# Revit family: Faucet_Touchless-Lavatory-KOHLER-Strayt-K-104S36-1
name_source: partatom
category: Plumbing Fixtures
units: mm (PartAtom-declared; Revit-internal decimal feet)

## family parameters
Cut with Voids When Loaded = No
Host = Face
Maintain Annotation Orientation = No
OmniClass Number = 23.31.11.00
OmniClass Title = Faucets
Part Type = Normal
Room Calculation Point = No
Round Connector Dimension = Use Diameter
Shared = No

## types (2) — shared parameters
ADA Compliant = Yes
Assembly Code = D2010
CW Connection = Yes
Cold Water Inlet = Cold Water Inlet
Date Modified = 06/20/2025
Default Elevation = 36"
Drain Included = Yes
Finish = Kohler-Metal-CP-Polished_Chrome
HW Connection = Yes
Height = 5 7/16"
Hot Water Inlet = Hot Water Inlet
Length = 5 3/16"
Manufacturer = Kohler Co.
Master Format 2014 = 22 41 39
Master Format 2014 Name = Residential Faucets, Supplies, and Trim
Material = Premium Metal Construction
Pressure = 60.00 psi
Product Documentation Link = https://www.us.kohler.com
Product Name = Strayt
Product Page URL = http://www.us.kohler.com
Spout Reach = 5 3/16"
Tempered Water Inlet = Tempered Water Inlet
URL = https://www.us.kohler.com
Vent Connection = No
Waste Connection = No
Waste Water Outlet = Waste Water Outlet
WaterSense Certified = No
Width = 2 1/16"

## per-type parameters (varying)
| type | Connector Diameter For Cold Water Inlet | Description | Distance 1 | Flow Rate | Model | Type |
| 0.35 GPM, CP-Polished Chrome | 3/8" | Touchless single hole lavatory faucet with Kinesis sensor technology, DC-powered, 0.35 gpm | 3/8" | 0 GPM | K-104S36-SATA-CP | 1 |
| 0.50 GPM, CP-Polished Chrome | 0" | Touchless single hole lavatory faucet with Kinesis sensor technology, DC-powered, 0.5 gpm | 0" | 1 GPM | K-104S36-SANA-CP | 2 |

## geometry (parser evidence)
native form markers: Sweep x5
no freeform markers — native parametric forms only
